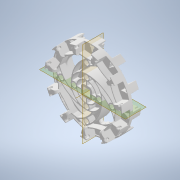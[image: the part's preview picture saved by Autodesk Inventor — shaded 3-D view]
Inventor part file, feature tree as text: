
AUTODESK INVENTOR PART (.ipt)
format: ipt  version: 2020 (Build 240168000, 168)  size: 11,475,456 bytes
history: native  units: in
note: dims shown in document units (in); Inventor stores cm internally (conversion verified against a paired STEP export)
features: plane x2, other x1, chamfer x1
ambient origin geometry x8: Origin, YZ Plane, XZ Plane, XY Plane, X Axis, Y Axis, Z Axis, Center Point
bodies: Solid1 (feature_tree)
feature tree (4):
  other  "Work Axis1"
  plane  "Work Plane1"
  plane  "Work Plane2"
  chamfer  "Chamfer2"  [1 undecoded]
note: 1 required parameter value undecoded (feature->parameter linkage not recoverable at this tier; creation-order binding heuristic only, values carry confidence <= 0.55)
